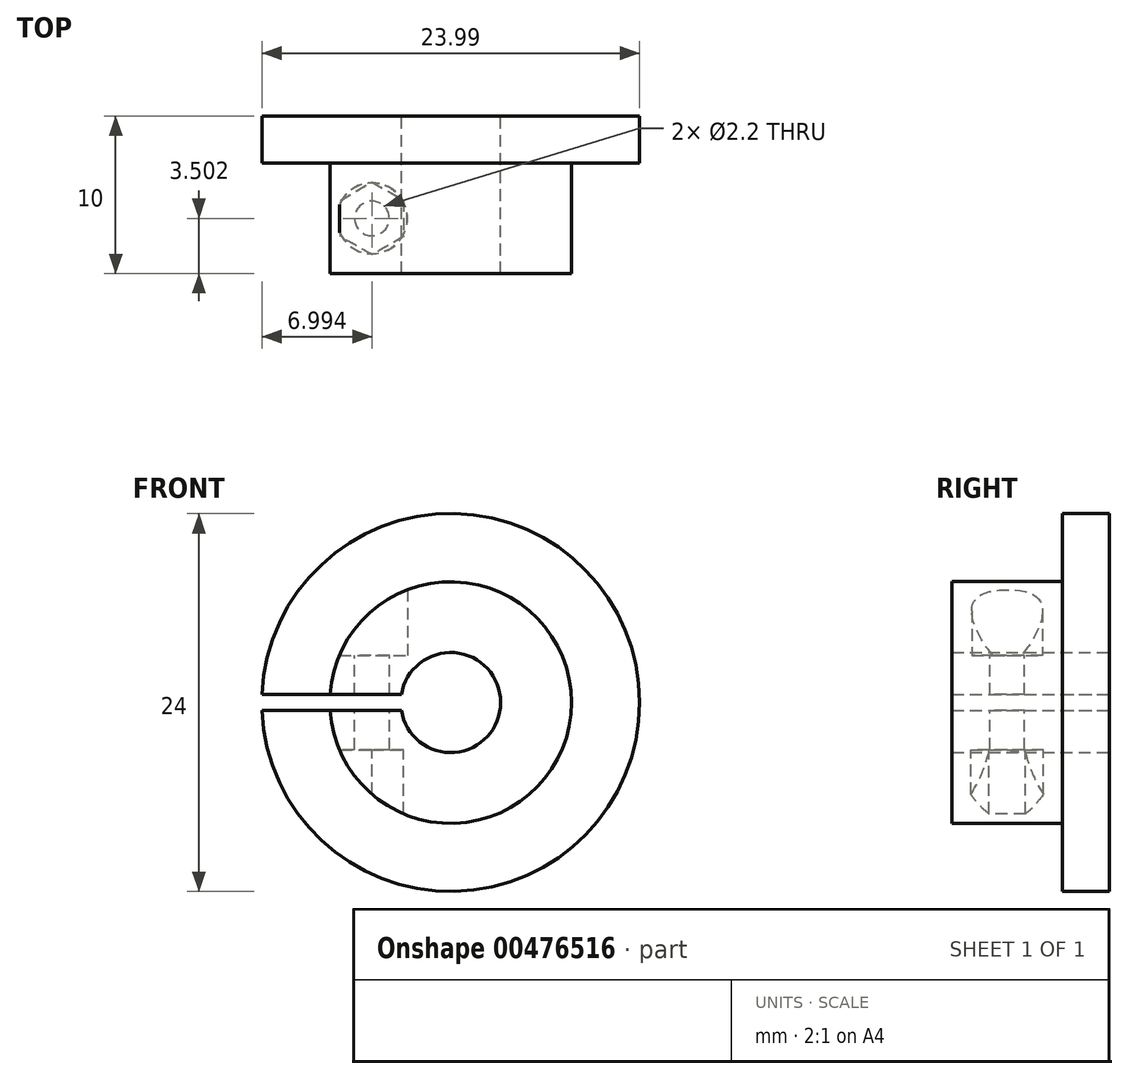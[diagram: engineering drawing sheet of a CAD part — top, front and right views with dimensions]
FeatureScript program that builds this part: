
annotation { "Feature Type Name" : "Feature", "Feature Type Description" : "" }
export const myFeature = defineFeature(function(context is Context, id is Id, definition is map)
    precondition{}
    {
        {
            var Q0;
            Q0=qCreatedBy(makeId("Front.planeOp"),FACE);
            var sketch = newSketch(context, id + "F0", { "sketchPlane" : qUnion([Q0])});
            skCircle(sketch, "E0", {"center": v(0, 0) * mm, "radius": 3.18 * mm});
            skCircle(sketch, "E1", {"center": v(0, 0) * mm, "radius": 12 * mm});
            skCircle(sketch, "E2", {"center": v(0, 0) * mm, "radius": 7.68 * mm});
            skSolve(sketch);
        }
        {
            var Q0;
            Q0=makeQuery(id+"F0.imprint","IMPRINT",FACE,{"disambiguationData":[TD([[makeQuery(id+"F0.imprint","IMPRINT",EDGE,{"derivedFrom":sQuery(id+"F0.wireOp",EDGE,"E0")}),-1.0]])]});
            extrude(context, id + "F1", {"entities" : qUnion([Q0]), "depth" : 10 * mm});
        }
        {
            var Q0;
            Q0=makeQuery(id+"F0.imprint","IMPRINT",FACE,{"disambiguationData":[TD([[makeQuery(id+"F0.imprint","IMPRINT",EDGE,{"derivedFrom":sQuery(id+"F0.wireOp",EDGE,"E1")}),1.0]])]});
            extrude(context, id + "F2", {"entities" : qUnion([Q0]), "operationType" : NewBodyOperationType.ADD, "depth" : 3 * mm});
        }
        {
            var Q0;
            Q0=qCreatedBy(makeId("Top.planeOp"),FACE);
            cPlane(context, id + "F3", {"entities" : qUnion([Q0]), "cplaneType" : CPlaneType.OFFSET, "offset" : 3 * mm, "width" : 150 * mm, "height" : 150 * mm});
        }
        {
            var Q0;
            Q0=qCreatedBy(id+"F3.planeOp",FACE);
            var sketch = newSketch(context, id + "F4", { "sketchPlane" : qUnion([Q0])});
            skLineSegment(sketch, "E3.0", {"start": v(7.68, -10) * mm, "end": v(-7.68, -10) * mm, "construction": true});
            skLineSegment(sketch, "E4", {"start": v(7.68, -3) * mm, "end": v(7.68, -10) * mm, "construction": true});
            skLineSegment(sketch, "E5", {"start": v(-7.68, -10) * mm, "end": v(-7.68, -3) * mm, "construction": true});
            skLineSegment(sketch, "E6", {"start": v(-6.78, -3) * mm, "end": v(8.57, -2.99) * mm, "construction": true});
            skLineSegment(sketch, "E7", {"start": v(-5, -3) * mm, "end": v(-5, -10) * mm, "construction": true});
            skPoint(sketch, "E8", {"position": v(-5, -6.5) * mm});
            skCircle(sketch, "E9", {"center": v(-5, -6.5) * mm, "radius": 2.25 * mm});
            skLineSegment(sketch, "E10", {"start": v(0, 0) * mm, "end": v(0, -10) * mm, "construction": true});
            skSolve(sketch);
        }
        {
            var Q0;
            Q0=makeQuery(id+"F4.imprint","IMPRINT",FACE,{"disambiguationData":[TD([[makeQuery(id+"F4.imprint","IMPRINT",EDGE,{"derivedFrom":sQuery(id+"F4.wireOp",EDGE,"E9")}),1.0]])]});
            extrude(context, id + "F5", {"entities" : qUnion([Q0]), "operationType" : NewBodyOperationType.REMOVE, "depth" : 25 * mm});
        }
        {
            var Q0;
            Q0=sQuery(id+"F4.wireOp",VERTEX,"E8");
            var Q1;
            Q1=makeQuery(id+"F1.opExtrude","SWEPT_BODY",BODY,{"disambiguationData":[OSD([sQuery(id+"F0.wireOp",EDGE,"E0"),sQuery(id+"F0.wireOp",EDGE,"E2")])]});
            hole(context, id + "F6", {"style" : HoleStyle.SIMPLE, "endStyle" : HoleEndStyle.BLIND, "holeDiameter" : 2.2 * mm, "holeDepth" : 16 * mm, "tappedDepth" : 13.9 * mm, "tapClearance" : 3, "startFromSketch" : true, "locations" : qUnion([Q0]), "scope" : qUnion([Q1])});
        }
        {
            var Q0;
            Q0=qCreatedBy(makeId("Top.planeOp"),FACE);
            cPlane(context, id + "F7", {"entities" : qUnion([Q0]), "cplaneType" : CPlaneType.OFFSET, "offset" : 3 * mm, "oppositeDirection" : true, "width" : 150 * mm, "height" : 150 * mm});
        }
        {
            var Q0;
            Q0=qCreatedBy(id+"F7.planeOp",FACE);
            var sketch = newSketch(context, id + "F8", { "sketchPlane" : qUnion([Q0])});
            skPoint(sketch, "E11.0", {"position": v(-5, -6.5) * mm});
            skCircle(sketch, "E12.cCircle", {"center": v(-5, -6.5) * mm, "radius": 2 * mm, "construction": true});
            skLineSegment(sketch, "E12.0", {"start": v(-3, -7.64) * mm, "end": v(-4.98, -8.8) * mm});
            skLineSegment(sketch, "E12.1", {"start": v(-4.98, -8.8) * mm, "end": v(-7, -7.66) * mm});
            skLineSegment(sketch, "E12.2", {"start": v(-7, -7.66) * mm, "end": v(-7, -5.35) * mm});
            skLineSegment(sketch, "E12.3", {"start": v(-7, -5.35) * mm, "end": v(-5, -4.19) * mm});
            skLineSegment(sketch, "E12.4", {"start": v(-5, -4.19) * mm, "end": v(-3, -5.33) * mm});
            skLineSegment(sketch, "E12.5", {"start": v(-3, -5.33) * mm, "end": v(-3, -7.64) * mm});
            skPoint(sketch, "E12.0.midPoint", {"position": v(-3.99, -8.23) * mm});
            skSolve(sketch);
        }
        {
            var Q0;
            Q0=makeQuery(id+"F8.imprint","IMPRINT",FACE,{"disambiguationData":[TD([[makeQuery(id+"F8.imprint","IMPRINT",EDGE,{"derivedFrom":sQuery(id+"F8.wireOp",EDGE,"E12.0")}),-1.0]])]});
            extrude(context, id + "F9", {"entities" : qUnion([Q0]), "operationType" : NewBodyOperationType.REMOVE, "oppositeDirection" : true, "depth" : 25 * mm});
        }
        {
            var Q0;
            Q0=qCreatedBy(makeId("Top.planeOp"),FACE);
            var sketch = newSketch(context, id + "F10", { "sketchPlane" : qUnion([Q0])});
            skLineSegment(sketch, "E13.0", {"start": v(7.68, -10) * mm, "end": v(-7.68, -10) * mm});
            skLineSegment(sketch, "E14.0", {"start": v(12, 0) * mm, "end": v(-12, 0) * mm});
            skLineSegment(sketch, "E15.bottom", {"start": v(-12, 0) * mm, "end": v(12, 0) * mm});
            skLineSegment(sketch, "E15.top", {"start": v(-12, -12.3) * mm, "end": v(12, -12.3) * mm});
            skLineSegment(sketch, "E15.left", {"start": v(-12, 0) * mm, "end": v(-12, -12.3) * mm});
            skLineSegment(sketch, "E15.right", {"start": v(12, 0) * mm, "end": v(12, -12.3) * mm});
            skLineSegment(sketch, "E16", {"start": v(0, 0) * mm, "end": v(0, -12.3) * mm});
            skSolve(sketch);
        }
        {
            var Q0;
            {var subQ4=sQuery(id+"F10.wireOp",EDGE,"E15.left");Q0=makeQuery(id+"F10.imprint","IMPRINT",FACE,{"disambiguationData":[TD([[makeQuery(id+"F10.imprint","IMPRINT",EDGE,{"derivedFrom":subQ4}),1.0]])]});}
            extrude(context, id + "F11", {"entities" : qUnion([Q0]), "operationType" : NewBodyOperationType.REMOVE, "endBound" : BoundingType.SYMMETRIC, "oppositeDirection" : true, "depth" : 1 * mm});
        }
    });
